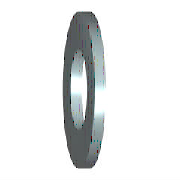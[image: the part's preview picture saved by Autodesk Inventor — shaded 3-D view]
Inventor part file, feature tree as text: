
AUTODESK INVENTOR PART (.ipt)
format: ipt  version: 2024.2 (Build 282272000, 272)  size: 105,984 bytes
history: native  units: mm (DEFAULTED — no unit token found)
features: other x1, plane x1
ambient origin geometry x7: Origin, YZ Plane, XY Plane, X Axis, Y Axis, Z Axis, Center Point
bodies: Solid1 (feature_tree), Body (feature_tree)
feature tree (2):
  other  "Work Axis1"
  plane  "Work Plane1"
